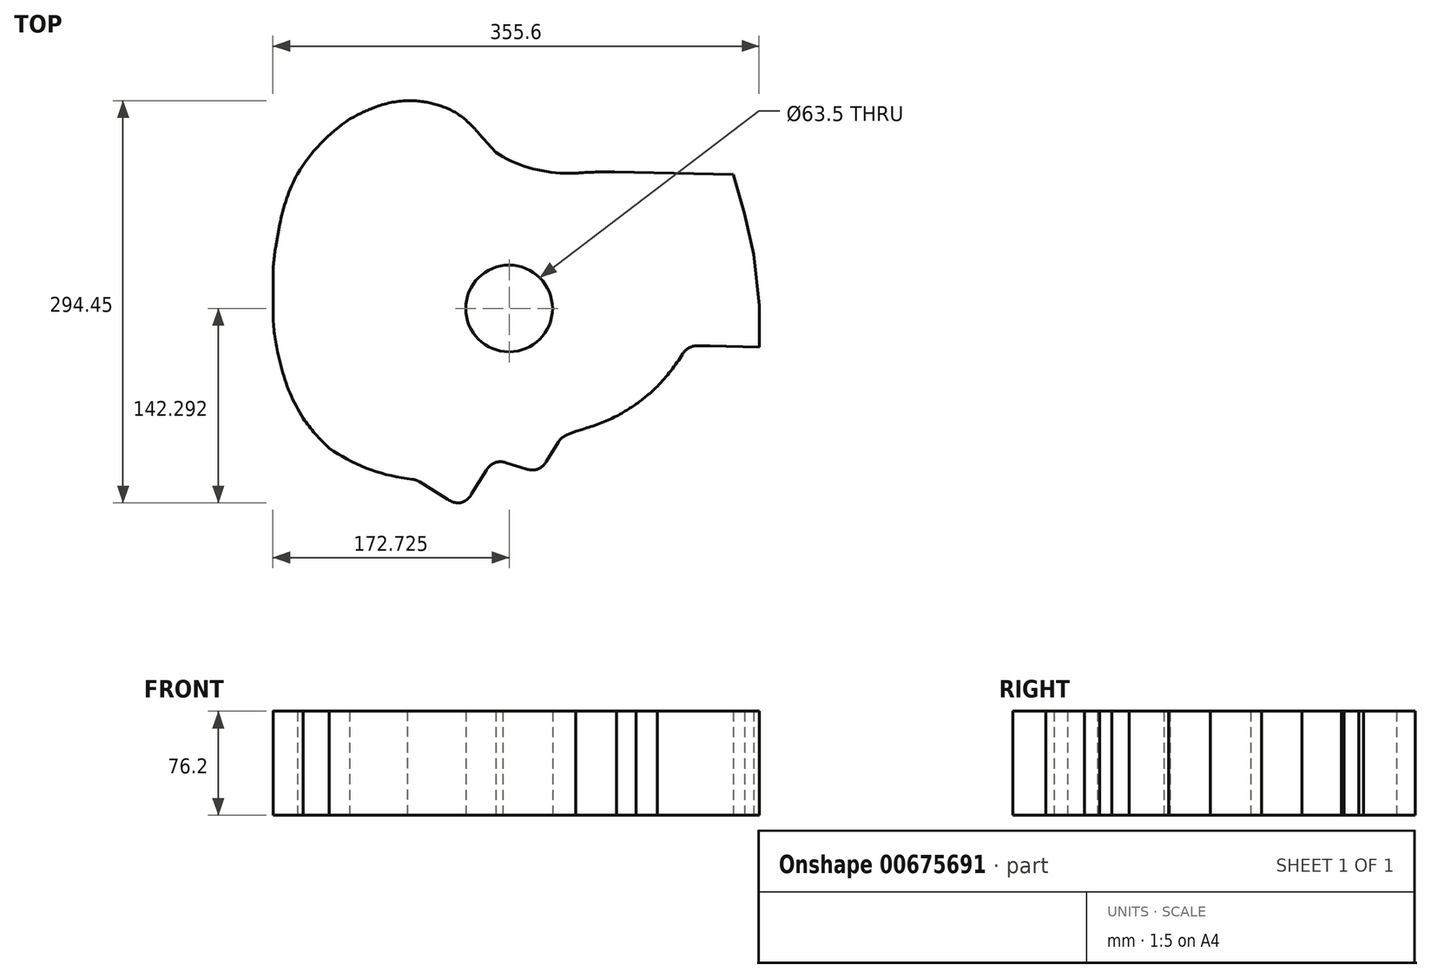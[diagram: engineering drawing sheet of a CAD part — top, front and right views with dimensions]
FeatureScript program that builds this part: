
annotation { "Feature Type Name" : "Feature", "Feature Type Description" : "" }
export const myFeature = defineFeature(function(context is Context, id is Id, definition is map)
    precondition{}
    {
        {
            var Q0;
            Q0=qCreatedBy(makeId("Top.planeOp"),FACE);
            var sketch = newSketch(context, id + "F0", { "sketchPlane" : qUnion([Q0])});
            skLineSegment(sketch, "E0", {"start": v(-69.97, -134.01) * mm, "end": v(-112.13, -128.47) * mm});
            skLineSegment(sketch, "E1", {"start": v(-112.13, -128.47) * mm, "end": v(-143.2, -103.5) * mm});
            skLineSegment(sketch, "E2", {"start": v(-143.2, -103.5) * mm, "end": v(-163.72, -72.43) * mm});
            skLineSegment(sketch, "E3", {"start": v(-163.72, -72.43) * mm, "end": v(-174.82, -25.84) * mm});
            skLineSegment(sketch, "E4", {"start": v(-174.82, -25.84) * mm, "end": v(-174.82, 25.2) * mm});
            skLineSegment(sketch, "E5", {"start": v(-174.82, 25.2) * mm, "end": v(-165.94, 74.02) * mm});
            skLineSegment(sketch, "E6", {"start": v(-165.94, 74.02) * mm, "end": v(-142.64, 115.07) * mm});
            skLineSegment(sketch, "E7", {"start": v(-142.64, 115.07) * mm, "end": v(-101.59, 140.6) * mm});
            skLineSegment(sketch, "E8", {"start": v(-101.59, 140.6) * mm, "end": v(-71.08, 146.14) * mm});
            skLineSegment(sketch, "E9", {"start": v(-71.08, 146.14) * mm, "end": v(-46.67, 140.6) * mm});
            skLineSegment(sketch, "E10", {"start": v(-46.67, 140.6) * mm, "end": v(-30.58, 126.72) * mm});
            skLineSegment(sketch, "E11", {"start": v(-30.58, 126.72) * mm, "end": v(-11.72, 105.64) * mm});
            skLineSegment(sketch, "E12", {"start": v(-11.72, 105.64) * mm, "end": v(9.35, 91.61) * mm});
            skLineSegment(sketch, "E13", {"start": v(9.35, 91.61) * mm, "end": v(33.2, 83.29) * mm});
            skLineSegment(sketch, "E14", {"start": v(33.2, 83.29) * mm, "end": v(59.83, 91.61) * mm});
            skLineSegment(sketch, "E15", {"start": v(59.83, 91.61) * mm, "end": v(161.9, 89.4) * mm});
            skLineSegment(sketch, "E16", {"start": v(161.9, 89.4) * mm, "end": v(170.23, 60.54) * mm});
            skLineSegment(sketch, "E17", {"start": v(170.23, 60.54) * mm, "end": v(176.89, 31.14) * mm});
            skLineSegment(sketch, "E18", {"start": v(176.89, 31.14) * mm, "end": v(180.78, -6.42) * mm});
            skLineSegment(sketch, "E19", {"start": v(180.78, -6.42) * mm, "end": v(180.78, -36.93) * mm});
            skLineSegment(sketch, "E20", {"start": v(180.78, -36.93) * mm, "end": v(144.7, -36.15) * mm});
            skLineSegment(sketch, "E21", {"start": v(-69.97, -134.01) * mm, "end": v(-36.13, -155.1) * mm});
            skLineSegment(sketch, "E22", {"start": v(-36.13, -155.1) * mm, "end": v(-13.46, -118.7) * mm});
            skLineSegment(sketch, "E23", {"start": v(-13.46, -118.7) * mm, "end": v(19.9, -129.02) * mm});
            skLineSegment(sketch, "E24", {"start": v(19.9, -129.02) * mm, "end": v(36.13, -102.97) * mm});
            skLineSegment(sketch, "E25", {"start": v(36.13, -102.97) * mm, "end": v(46.53, -98.5) * mm});
            skLineSegment(sketch, "E26", {"start": v(46.53, -98.5) * mm, "end": v(65.95, -92.96) * mm});
            skLineSegment(sketch, "E27", {"start": v(65.95, -92.96) * mm, "end": v(83.15, -84.08) * mm});
            skLineSegment(sketch, "E28", {"start": v(83.15, -84.08) * mm, "end": v(100.34, -71.88) * mm});
            skLineSegment(sketch, "E29", {"start": v(100.34, -71.88) * mm, "end": v(115.88, -56.35) * mm});
            skLineSegment(sketch, "E30", {"start": v(115.88, -56.35) * mm, "end": v(128.64, -35.82) * mm});
            skLineSegment(sketch, "E31", {"start": v(128.64, -35.82) * mm, "end": v(144.7, -36.15) * mm});
            skCircle(sketch, "E32", {"center": v(-2.1, -8.67) * mm, "radius": 31.75 * mm});
            skSolve(sketch);
        }
        {
            var Q0;
            Q0=makeQuery(id+"F0.imprint","IMPRINT",FACE,{"disambiguationData":[TD([[makeQuery(id+"F0.imprint","IMPRINT",EDGE,{"derivedFrom":sQuery(id+"F0.wireOp",EDGE,"E0")}),-1.0]])]});
            extrude(context, id + "F1", {"entities" : qUnion([Q0]), "depth" : 101.6 * mm, "offsetDistance" : 25.4 * mm});
        }
        {
            var Q0;
            Q0=makeQuery(id+"F1.opExtrude","SWEPT_EDGE",EDGE,{"disambiguationData":[OSD([sQuery(id+"F0.wireOp",EDGE,"E7"),sQuery(id+"F0.wireOp",EDGE,"E8")])]});
            var Q1;
            Q1=makeQuery(id+"F1.opExtrude","SWEPT_EDGE",EDGE,{"disambiguationData":[OSD([sQuery(id+"F0.wireOp",EDGE,"E6"),sQuery(id+"F0.wireOp",EDGE,"E7")])]});
            var Q2;
            Q2=makeQuery(id+"F1.opExtrude","SWEPT_EDGE",EDGE,{"disambiguationData":[OSD([sQuery(id+"F0.wireOp",EDGE,"E5"),sQuery(id+"F0.wireOp",EDGE,"E6")])]});
            var Q3;
            Q3=makeQuery(id+"F1.opExtrude","SWEPT_EDGE",EDGE,{"disambiguationData":[OSD([sQuery(id+"F0.wireOp",EDGE,"E4"),sQuery(id+"F0.wireOp",EDGE,"E5")])]});
            var Q4;
            Q4=makeQuery(id+"F1.opExtrude","SWEPT_EDGE",EDGE,{"disambiguationData":[OSD([sQuery(id+"F0.wireOp",EDGE,"E3"),sQuery(id+"F0.wireOp",EDGE,"E4")])]});
            var Q5;
            Q5=makeQuery(id+"F1.opExtrude","SWEPT_EDGE",EDGE,{"disambiguationData":[OSD([sQuery(id+"F0.wireOp",EDGE,"E2"),sQuery(id+"F0.wireOp",EDGE,"E3")])]});
            var Q6;
            Q6=makeQuery(id+"F1.opExtrude","SWEPT_EDGE",EDGE,{"disambiguationData":[OSD([sQuery(id+"F0.wireOp",EDGE,"E1"),sQuery(id+"F0.wireOp",EDGE,"E2")])]});
            var Q7;
            Q7=makeQuery(id+"F1.opExtrude","SWEPT_EDGE",EDGE,{"disambiguationData":[OSD([sQuery(id+"F0.wireOp",EDGE,"E0"),sQuery(id+"F0.wireOp",EDGE,"E1")])]});
            var Q8;
            Q8=makeQuery(id+"F1.opExtrude","SWEPT_EDGE",EDGE,{"disambiguationData":[OSD([sQuery(id+"F0.wireOp",EDGE,"E8"),sQuery(id+"F0.wireOp",EDGE,"E9")])]});
            fillet(context, id + "F2", {"entities" : qUnion([Q0, Q1, Q2, Q3, Q4, Q5, Q6, Q7, Q8]), "radius" : 127 * mm, "tangentPropagation" : true, "allowEdgeOverflow" : false});
        }
        {
            var Q0;
            Q0=makeQuery(id+"F1.opExtrude","SWEPT_EDGE",EDGE,{"disambiguationData":[OSD([sQuery(id+"F0.wireOp",EDGE,"E26"),sQuery(id+"F0.wireOp",EDGE,"E27")])]});
            var Q1;
            Q1=makeQuery(id+"F1.opExtrude","SWEPT_EDGE",EDGE,{"disambiguationData":[OSD([sQuery(id+"F0.wireOp",EDGE,"E27"),sQuery(id+"F0.wireOp",EDGE,"E28")])]});
            var Q2;
            Q2=makeQuery(id+"F1.opExtrude","SWEPT_EDGE",EDGE,{"disambiguationData":[OSD([sQuery(id+"F0.wireOp",EDGE,"E28"),sQuery(id+"F0.wireOp",EDGE,"E29")])]});
            var Q3;
            Q3=makeQuery(id+"F1.opExtrude","SWEPT_EDGE",EDGE,{"disambiguationData":[OSD([sQuery(id+"F0.wireOp",EDGE,"E29"),sQuery(id+"F0.wireOp",EDGE,"E30")])]});
            fillet(context, id + "F3", {"entities" : qUnion([Q0, Q1, Q2, Q3]), "radius" : 152.4 * mm, "tangentPropagation" : true, "allowEdgeOverflow" : false});
        }
        {
            var Q0;
            Q0=makeQuery(id+"F1.opExtrude","SWEPT_EDGE",EDGE,{"disambiguationData":[OSD([sQuery(id+"F0.wireOp",EDGE,"E13"),sQuery(id+"F0.wireOp",EDGE,"E14")])]});
            var Q1;
            Q1=makeQuery(id+"F1.opExtrude","SWEPT_EDGE",EDGE,{"disambiguationData":[OSD([sQuery(id+"F0.wireOp",EDGE,"E12"),sQuery(id+"F0.wireOp",EDGE,"E13")])]});
            var Q2;
            Q2=makeQuery(id+"F1.opExtrude","SWEPT_EDGE",EDGE,{"disambiguationData":[OSD([sQuery(id+"F0.wireOp",EDGE,"E10"),sQuery(id+"F0.wireOp",EDGE,"E11")])]});
            fillet(context, id + "F4", {"entities" : qUnion([Q0, Q1, Q2]), "radius" : 152.4 * mm, "tangentPropagation" : true, "allowEdgeOverflow" : false});
        }
        {
            var Q0;
            Q0=makeQuery(id+"F4.opFillet","BLEND_EDGE",EDGE,{"blendedFrom":[makeQuery(id+"F1.opExtrude","SWEPT_EDGE",EDGE,{"disambiguationData":[OSD([sQuery(id+"F0.wireOp",EDGE,"E13"),sQuery(id+"F0.wireOp",EDGE,"E14")])]}),makeQuery(id+"F1.opExtrude","SWEPT_FACE",FACE,{"disambiguationData":[OSD([sQuery(id+"F0.wireOp",EDGE,"E15")])]})],"blendedInto":[makeQuery(id+"F1.opExtrude","SWEPT_FACE",FACE,{"disambiguationData":[OSD([sQuery(id+"F0.wireOp",EDGE,"E15")])]})]});
            fillet(context, id + "F5", {"entities" : qUnion([Q0]), "radius" : 254 * mm, "tangentPropagation" : true, "allowEdgeOverflow" : false});
        }
        {
            var Q0;
            {var subQ0=sQuery(id+"F0.wireOp",EDGE,"E13");Q0=makeQuery(id+"F4.opFillet","BLEND_EDGE",EDGE,{"blendedFrom":[makeQuery(id+"F1.opExtrude","SWEPT_EDGE",EDGE,{"disambiguationData":[OSD([sQuery(id+"F0.wireOp",EDGE,"E12"),subQ0])]}),makeQuery(id+"F1.opExtrude","SWEPT_EDGE",EDGE,{"disambiguationData":[OSD([subQ0,sQuery(id+"F0.wireOp",EDGE,"E14")])]})],"blendedInto":[]});}
            fillet(context, id + "F6", {"entities" : qUnion([Q0]), "radius" : 101.6 * mm, "tangentPropagation" : true, "allowEdgeOverflow" : false});
        }
        {
            var Q0;
            Q0=makeQuery(id+"F2.opFillet","BLEND_EDGE",EDGE,{"blendedFrom":[makeQuery(id+"F1.opExtrude","SWEPT_EDGE",EDGE,{"disambiguationData":[OSD([sQuery(id+"F0.wireOp",EDGE,"E8"),sQuery(id+"F0.wireOp",EDGE,"E9")])]}),makeQuery(id+"F1.opExtrude","SWEPT_FACE",FACE,{"disambiguationData":[OSD([sQuery(id+"F0.wireOp",EDGE,"E10")])]})],"blendedInto":[makeQuery(id+"F1.opExtrude","SWEPT_FACE",FACE,{"disambiguationData":[OSD([sQuery(id+"F0.wireOp",EDGE,"E10")])]})]});
            fillet(context, id + "F7", {"entities" : qUnion([Q0]), "radius" : 76.2 * mm, "tangentPropagation" : true, "rho" : 0.5, "crossSection" : FilletCrossSection.CONIC, "allowEdgeOverflow" : false});
        }
        {
            var Q0;
            {var subQ0=sQuery(id+"F0.wireOp",EDGE,"E10");Q0=makeQuery(id+"F7.opFillet","BLEND_EDGE",EDGE,{"blendedFrom":[makeQuery(id+"F2.opFillet","BLEND_EDGE",EDGE,{"blendedFrom":[makeQuery(id+"F1.opExtrude","SWEPT_EDGE",EDGE,{"disambiguationData":[OSD([sQuery(id+"F0.wireOp",EDGE,"E8"),sQuery(id+"F0.wireOp",EDGE,"E9")])]}),makeQuery(id+"F1.opExtrude","SWEPT_FACE",FACE,{"disambiguationData":[OSD([subQ0])]})],"blendedInto":[makeQuery(id+"F1.opExtrude","SWEPT_FACE",FACE,{"disambiguationData":[OSD([subQ0])]})]}),makeQuery(id+"F4.opFillet","BLEND_FACE",FACE,{"disambiguationData":[OSD([subQ0,sQuery(id+"F0.wireOp",EDGE,"E11")])]})],"blendedInto":[makeQuery(id+"F4.opFillet","BLEND_FACE",FACE,{"disambiguationData":[OSD([subQ0,sQuery(id+"F0.wireOp",EDGE,"E11")])]})]});}
            fillet(context, id + "F8", {"entities" : qUnion([Q0]), "radius" : 50.8 * mm, "tangentPropagation" : true, "allowEdgeOverflow" : false});
        }
        {
            var Q0;
            {var subQ0=sQuery(id+"F0.wireOp",EDGE,"E8");Q0=makeQuery(id+"F2.opFillet","BLEND_EDGE",EDGE,{"blendedFrom":[makeQuery(id+"F1.opExtrude","SWEPT_EDGE",EDGE,{"disambiguationData":[OSD([sQuery(id+"F0.wireOp",EDGE,"E7"),subQ0])]}),makeQuery(id+"F1.opExtrude","SWEPT_EDGE",EDGE,{"disambiguationData":[OSD([subQ0,sQuery(id+"F0.wireOp",EDGE,"E9")])]})],"blendedInto":[]});}
            fillet(context, id + "F9", {"entities" : qUnion([Q0]), "radius" : 76.2 * mm, "tangentPropagation" : true, "allowEdgeOverflow" : false});
        }
        {
            var Q0;
            Q0=makeQuery(id+"F1.opExtrude","SWEPT_EDGE",EDGE,{"disambiguationData":[OSD([sQuery(id+"F0.wireOp",EDGE,"E23"),sQuery(id+"F0.wireOp",EDGE,"E24")])]});
            var Q1;
            Q1=makeQuery(id+"F1.opExtrude","SWEPT_EDGE",EDGE,{"disambiguationData":[OSD([sQuery(id+"F0.wireOp",EDGE,"E22"),sQuery(id+"F0.wireOp",EDGE,"E23")])]});
            var Q2;
            Q2=makeQuery(id+"F1.opExtrude","SWEPT_EDGE",EDGE,{"disambiguationData":[OSD([sQuery(id+"F0.wireOp",EDGE,"E21"),sQuery(id+"F0.wireOp",EDGE,"E22")])]});
            var Q3;
            Q3=makeQuery(id+"F1.opExtrude","SWEPT_EDGE",EDGE,{"disambiguationData":[OSD([sQuery(id+"F0.wireOp",EDGE,"E30"),sQuery(id+"F0.wireOp",EDGE,"E31")])]});
            var Q4;
            Q4=makeQuery(id+"F1.opExtrude","SWEPT_EDGE",EDGE,{"disambiguationData":[OSD([sQuery(id+"F0.wireOp",EDGE,"E24"),sQuery(id+"F0.wireOp",EDGE,"E25")])]});
            var Q5;
            Q5=makeQuery(id+"F1.opExtrude","SWEPT_EDGE",EDGE,{"disambiguationData":[OSD([sQuery(id+"F0.wireOp",EDGE,"E0"),sQuery(id+"F0.wireOp",EDGE,"E21")])]});
            fillet(context, id + "F10", {"entities" : qUnion([Q0, Q1, Q2, Q3, Q4, Q5]), "radius" : 12.7 * mm, "tangentPropagation" : true, "rho" : 0.5, "crossSection" : FilletCrossSection.CONIC, "allowEdgeOverflow" : false});
        }
        {
            var Q0;
            Q0=makeQuery(id+"F1.opExtrude","CAP_FACE",FACE,{"disambiguationData":[OSD([sQuery(id+"F0.wireOp",EDGE,"E0"),sQuery(id+"F0.wireOp",EDGE,"E1"),sQuery(id+"F0.wireOp",EDGE,"E2"),sQuery(id+"F0.wireOp",EDGE,"E3"),sQuery(id+"F0.wireOp",EDGE,"E4"),sQuery(id+"F0.wireOp",EDGE,"E5"),sQuery(id+"F0.wireOp",EDGE,"E6"),sQuery(id+"F0.wireOp",EDGE,"E7"),sQuery(id+"F0.wireOp",EDGE,"E8"),sQuery(id+"F0.wireOp",EDGE,"E9"),sQuery(id+"F0.wireOp",EDGE,"E10"),sQuery(id+"F0.wireOp",EDGE,"E11"),sQuery(id+"F0.wireOp",EDGE,"E12"),sQuery(id+"F0.wireOp",EDGE,"E13"),sQuery(id+"F0.wireOp",EDGE,"E14"),sQuery(id+"F0.wireOp",EDGE,"E15"),sQuery(id+"F0.wireOp",EDGE,"E16"),sQuery(id+"F0.wireOp",EDGE,"E17"),sQuery(id+"F0.wireOp",EDGE,"E18"),sQuery(id+"F0.wireOp",EDGE,"E19"),sQuery(id+"F0.wireOp",EDGE,"E20"),sQuery(id+"F0.wireOp",EDGE,"E21"),sQuery(id+"F0.wireOp",EDGE,"E22"),sQuery(id+"F0.wireOp",EDGE,"E23"),sQuery(id+"F0.wireOp",EDGE,"E24"),sQuery(id+"F0.wireOp",EDGE,"E25"),sQuery(id+"F0.wireOp",EDGE,"E26"),sQuery(id+"F0.wireOp",EDGE,"E27"),sQuery(id+"F0.wireOp",EDGE,"E28"),sQuery(id+"F0.wireOp",EDGE,"E29"),sQuery(id+"F0.wireOp",EDGE,"E30"),sQuery(id+"F0.wireOp",EDGE,"E31"),sQuery(id+"F0.wireOp",EDGE,"E32")])],"isStart":true});
            extrude(context, id + "F11", {"entities" : qUnion([Q0]), "operationType" : NewBodyOperationType.REMOVE, "oppositeDirection" : true, "depth" : 25.4 * mm, "offsetDistance" : 25.4 * mm});
        }
    });
